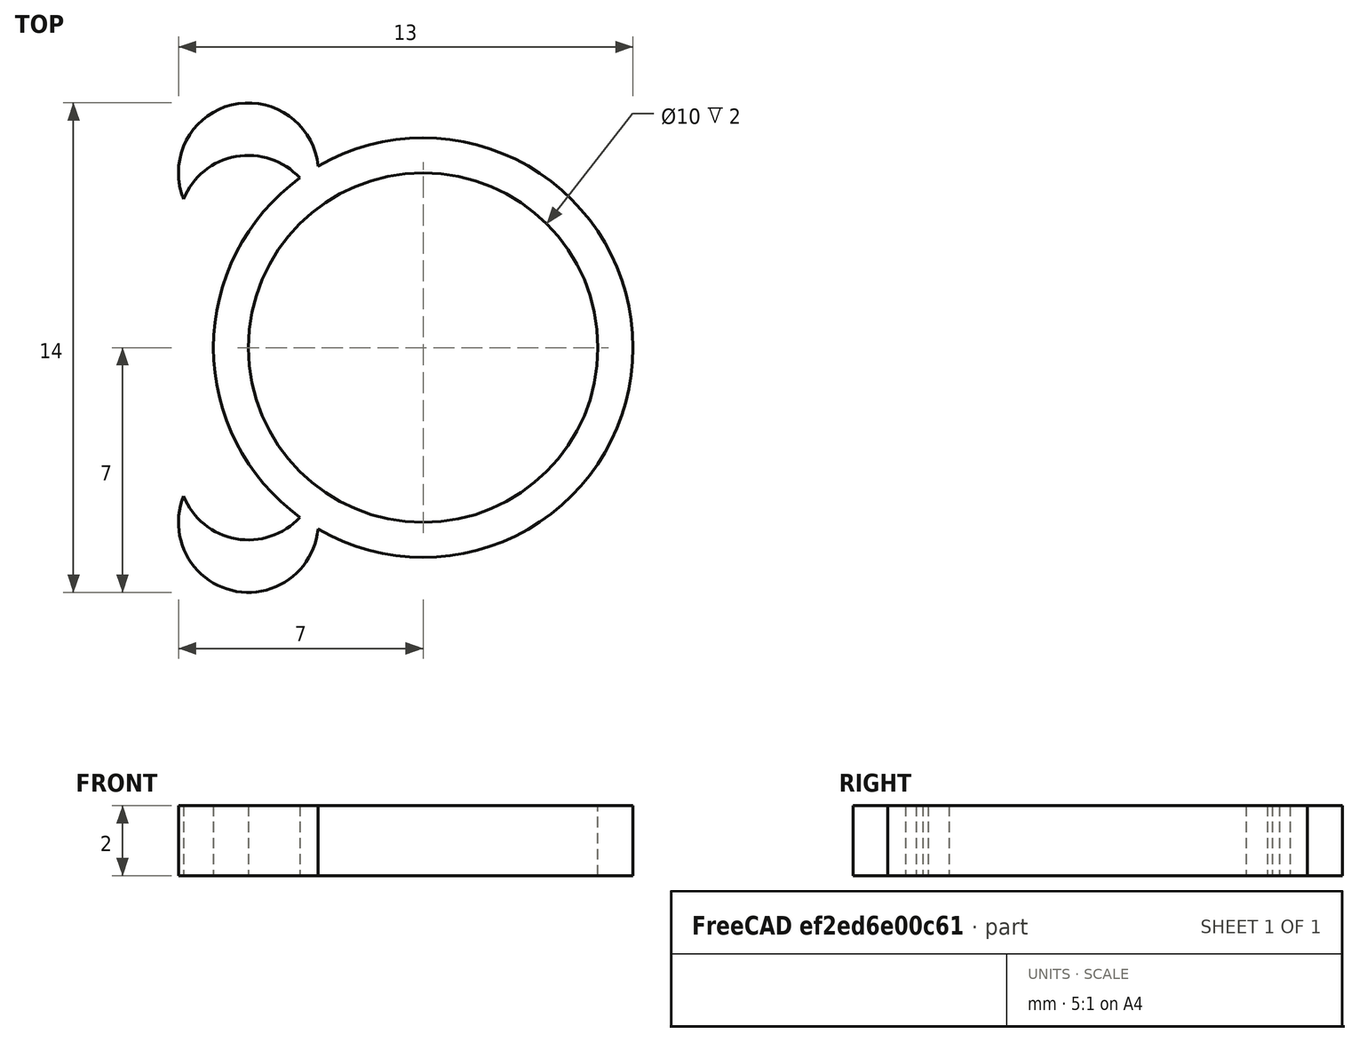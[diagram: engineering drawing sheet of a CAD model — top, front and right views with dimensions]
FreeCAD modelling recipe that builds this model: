
FCSTD DOCUMENT  (FreeCAD 0.21R33771 (Git))
Label: anillodemoniaco
License: All rights reserved
LicenseURL: https://en.wikipedia.org/wiki/All_rights_reserved
objects: Part::Cylinder×6, Part::Cut×3, Part::MultiFuse×1
note: 10 computed .brp shape members not serialized (recipe doc carries the construction recipe); baked Part::Feature solids carry a one-line shape summary decoded from their .brp

FEATURE [Part::Cylinder] Cylinder
  Angle = 360
  AttacherType = Attacher::AttachEngine3D
  FirstAngle = 0
  Height = 2
  Radius = 2
  SecondAngle = 0
FEATURE [Part::Cylinder] Cylinder001
  Angle = 360
  AttacherType = Attacher::AttachEngine3D
  FirstAngle = 0
  Height = 4
  Placement = pos=(0,1.5,0) rot=(0,0,1;0rad)
  Radius = 2
  SecondAngle = 0
FEATURE [Part::Cut] Cut
  Base = -> Cylinder
  Tool = -> Cylinder001
FEATURE [Part::Cylinder] Cylinder002
  Angle = 360
  AttacherType = Attacher::AttachEngine3D
  FirstAngle = 0
  Height = 2
  Radius = 2
  SecondAngle = 0
FEATURE [Part::Cylinder] Cylinder003
  Angle = 360
  AttacherType = Attacher::AttachEngine3D
  FirstAngle = 0
  Height = 4
  Placement = pos=(0,1.5,0) rot=(0,0,1;0rad)
  Radius = 2
  SecondAngle = 0
FEATURE [Part::Cut] Cut001
  Base = -> Cylinder002
  Placement = pos=(0,10,0) rot=(0,0,1;3.14159rad)
  Tool = -> Cylinder003
FEATURE [Part::Cylinder] Cylinder004
  Angle = 360
  AttacherType = Attacher::AttachEngine3D
  FirstAngle = 0
  Height = 2
  Placement = pos=(5,5,0) rot=(0,0,1;0rad)
  Radius = 6
  SecondAngle = 0
FEATURE [Part::Cylinder] Cylinder005
  Angle = 360
  AttacherType = Attacher::AttachEngine3D
  FirstAngle = 0
  Height = 3
  Placement = pos=(5,5,0) rot=(0,0,1;0rad)
  Radius = 5
  SecondAngle = 0
FEATURE [Part::MultiFuse] Fusion
  Shapes = -> [Cylinder004,Cut001,Cut]
FEATURE [Part::Cut] Cut002
  Base = -> Fusion
  Tool = -> Cylinder005
